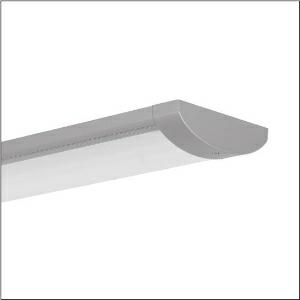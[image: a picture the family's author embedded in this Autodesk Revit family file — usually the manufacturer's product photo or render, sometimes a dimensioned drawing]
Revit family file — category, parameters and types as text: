
# Revit family: tv_20_5xa861d4n0x
name_source: partatom
category: Lighting Fixtures
units: mm (PartAtom-declared; Revit-internal decimal feet)

## family parameters
Cut with Voids When Loaded = No
Host = Face
Light Source = No
Part Type = Normal
Room Calculation Point = No
Round Connector Dimension = Use Diameter
Shared = No

## types (1)
- TV 20 (1 x LED 4000K / CRI = 80 (unbekannt), 5120 lm, 4000K)
    Apparent Load = 50 VA
    CIE Flux Codes = 48 78 95 99 100
    Color Rendering = 80
    Color Temperature = 4000K
    Default Elevation = 1800 mm
    Description = TV 20, vandal-proof luminaire, primary light control with specular reflector, of aluminium, matt, primary optical cover: enclosure, of PC, frosted, light emission: direct distribution, primary light characteristic: symmetric, installation type: surface-mounted, LED rated luminous flux: 5.120 lm, light colour: 840, colour temperature: 4000K, control gear: ECG DALI, mains connection: 230V, AC, 50Hz, rated input power: 50W, luminaire housing, of aluminium, coated, Siteco® metallic grey (DB 702S), length: 1.561 mm, width: 260 mm, height: 70mm, protection rating (complete): IP65, insulation class (complete): insulation class I (protective earthing), certification: CE, protection symbol: F, impact resistance: 2x IK10, standard: EN 60598, packaging unit: 1 piece
    Height = 70 mm
    Lamp = 1 x LED 4000K / CRI >= 80 (unbekannt)
    Lamp Light Flux = 5120 lm
    Lamp count = 1
    Length = 1561 mm
    Luminous efficacy = 102 lm/W
    Manufacturer = Siteco
    ModVariant = No
    Model = 5XA861D4N0X
    Mounting Place = Ceiling
    Mounting Type = Surface mounted
    Number of Poles = 1
    OnlyDefault = Yes
    Power Factor = 1
    Product Name = TV 20
    Product group = vandal-proof luminaire
    ProductGroupID = 307
    Protection Class = Protection class I
    Protection Degree = IP 65
    RLX_Detail_Level = 1
    RlxData = <blob elided: 25189 chars, md5=abcb7ba3>
    Socket = socket
    Standby Power = 0 W
    System Light Flux = 5120 lm
    System Power = 50 W
    Type Comments = Product without accessories
    Type Image = l_1004809.jpg
    URL = http://relux.com
    VarID = ---
    Voltage = 0 V
    Weight = 0.00 kg
    Width = 260 mm

## geometry (parser evidence)
native form markers: Blend x4, Sweep x10
no freeform markers — native parametric forms only
